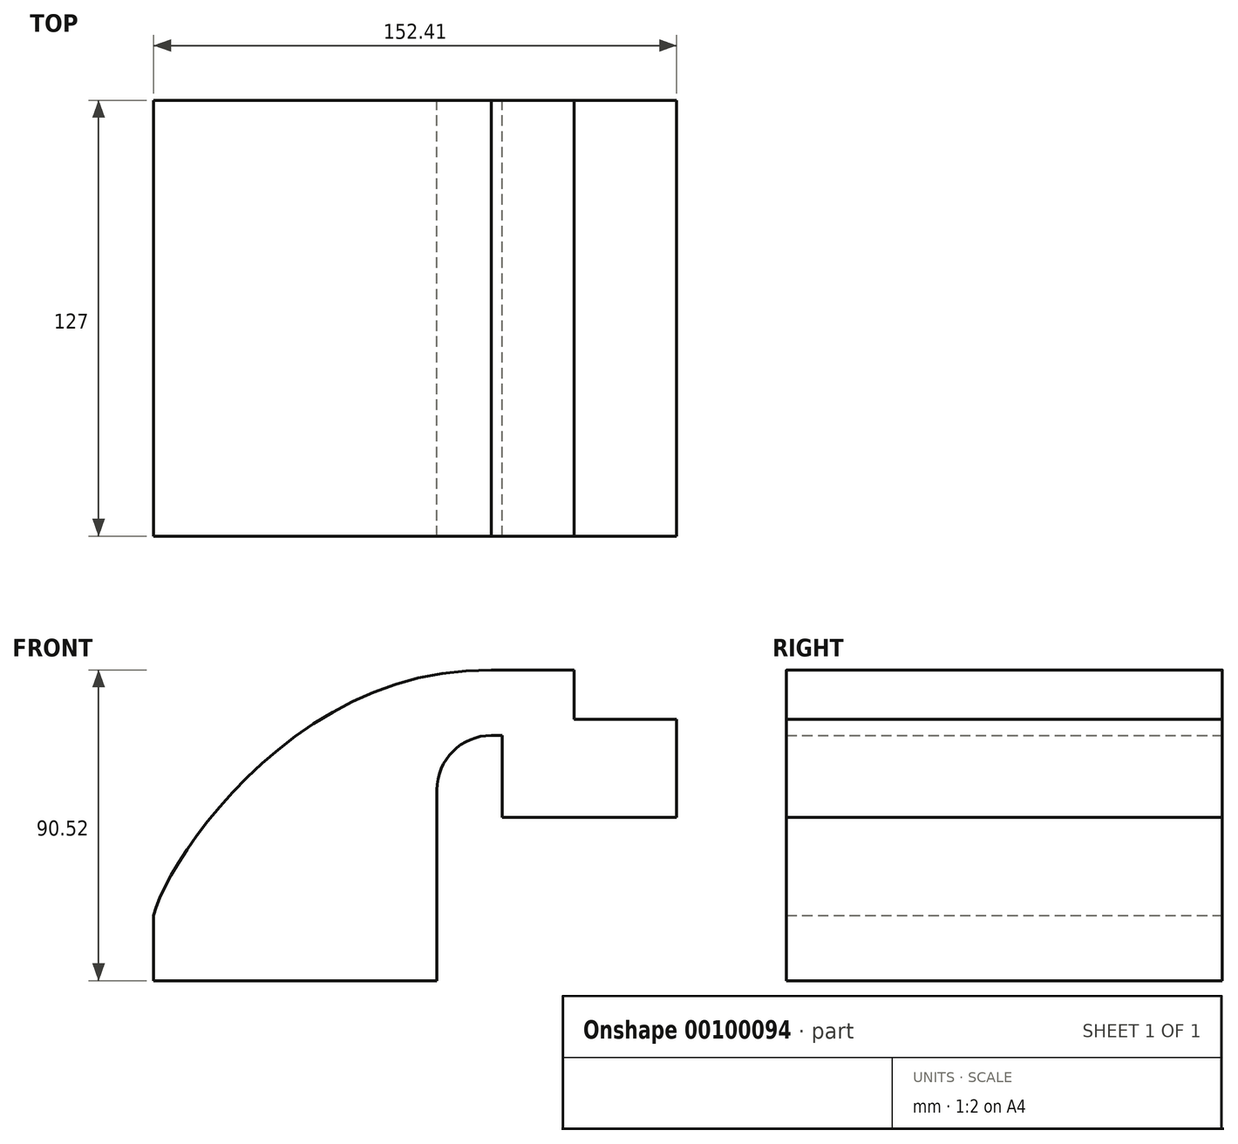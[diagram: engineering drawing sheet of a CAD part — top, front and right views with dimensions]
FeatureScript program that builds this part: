
annotation { "Feature Type Name" : "Feature", "Feature Type Description" : "" }
export const myFeature = defineFeature(function(context is Context, id is Id, definition is map)
    precondition{}
    {
        {
            var Q0;
            Q0=qCreatedBy(makeId("Front.planeOp"),FACE);
            var sketch = newSketch(context, id + "F0", { "sketchPlane" : qUnion([Q0])});
            skLineSegment(sketch, "E0.bottom", {"start": v(-41.28, 9.52) * mm, "end": v(41.27, 9.53) * mm});
            skLineSegment(sketch, "E0.top", {"start": v(-41.28, -9.53) * mm, "end": v(41.28, -9.53) * mm});
            skLineSegment(sketch, "E0.left", {"start": v(-41.28, 9.52) * mm, "end": v(-41.28, -9.53) * mm});
            skLineSegment(sketch, "E0.right", {"start": v(41.27, 9.53) * mm, "end": v(41.28, -9.52) * mm});
            skPoint(sketch, "E0.middle", {"position": v(0, 0) * mm});
            skLineSegment(sketch, "E1.bottom", {"start": v(111.12, 38.1) * mm, "end": v(60.32, 38.1) * mm});
            skLineSegment(sketch, "E1.top", {"start": v(111.12, 66.68) * mm, "end": v(60.32, 66.68) * mm});
            skLineSegment(sketch, "E1.left", {"start": v(111.12, 38.1) * mm, "end": v(111.12, 66.68) * mm});
            skLineSegment(sketch, "E1.right", {"start": v(60.32, 38.1) * mm, "end": v(60.32, 66.68) * mm});
            skPoint(sketch, "E1.middle", {"position": v(85.72, 52.39) * mm});
            skLineSegment(sketch, "E2", {"start": v(41.27, 9.53) * mm, "end": v(41.27, 46.05) * mm});
            skArc(sketch, "E3", {"start": v(41.27, 46.05) * mm, "mid": v(45.92, 57.28) * mm, "end": v(57.15, 61.93) * mm});
            skLineSegment(sketch, "E4", {"start": v(57.15, 61.93) * mm, "end": v(81.3, 61.93) * mm});
            skLineSegment(sketch, "E5.0", {"start": v(57.15, 80.98) * mm, "end": v(81.3, 80.98) * mm});
            skArc(sketch, "E5.1", {"start": v(22.22, 46.05) * mm, "mid": v(32.45, 70.75) * mm, "end": v(57.15, 80.98) * mm});
            skLineSegment(sketch, "E5.2", {"start": v(22.22, 9.53) * mm, "end": v(22.22, 46.05) * mm});
            skLineSegment(sketch, "E6", {"start": v(81.3, 61.93) * mm, "end": v(81.3, 80.98) * mm});
            skFitSpline(sketch, "E7", {"points": [v(-41.28, 9.52) * mm, v(57.15, 80.98) * mm], "startDerivative": vector(12.32, 48.68) * mm, "endDerivative": vector(171.45, -2.77) * mm});
            skSolve(sketch);
        }
        {
            var Q0;
            Q0 = qSketchRegion(id + "F0", true);
            extrude(context, id + "F1", {"entities" : qUnion([Q0]), "endBound" : BoundingType.SYMMETRIC, "depth" : 127 * mm});
        }
    });
